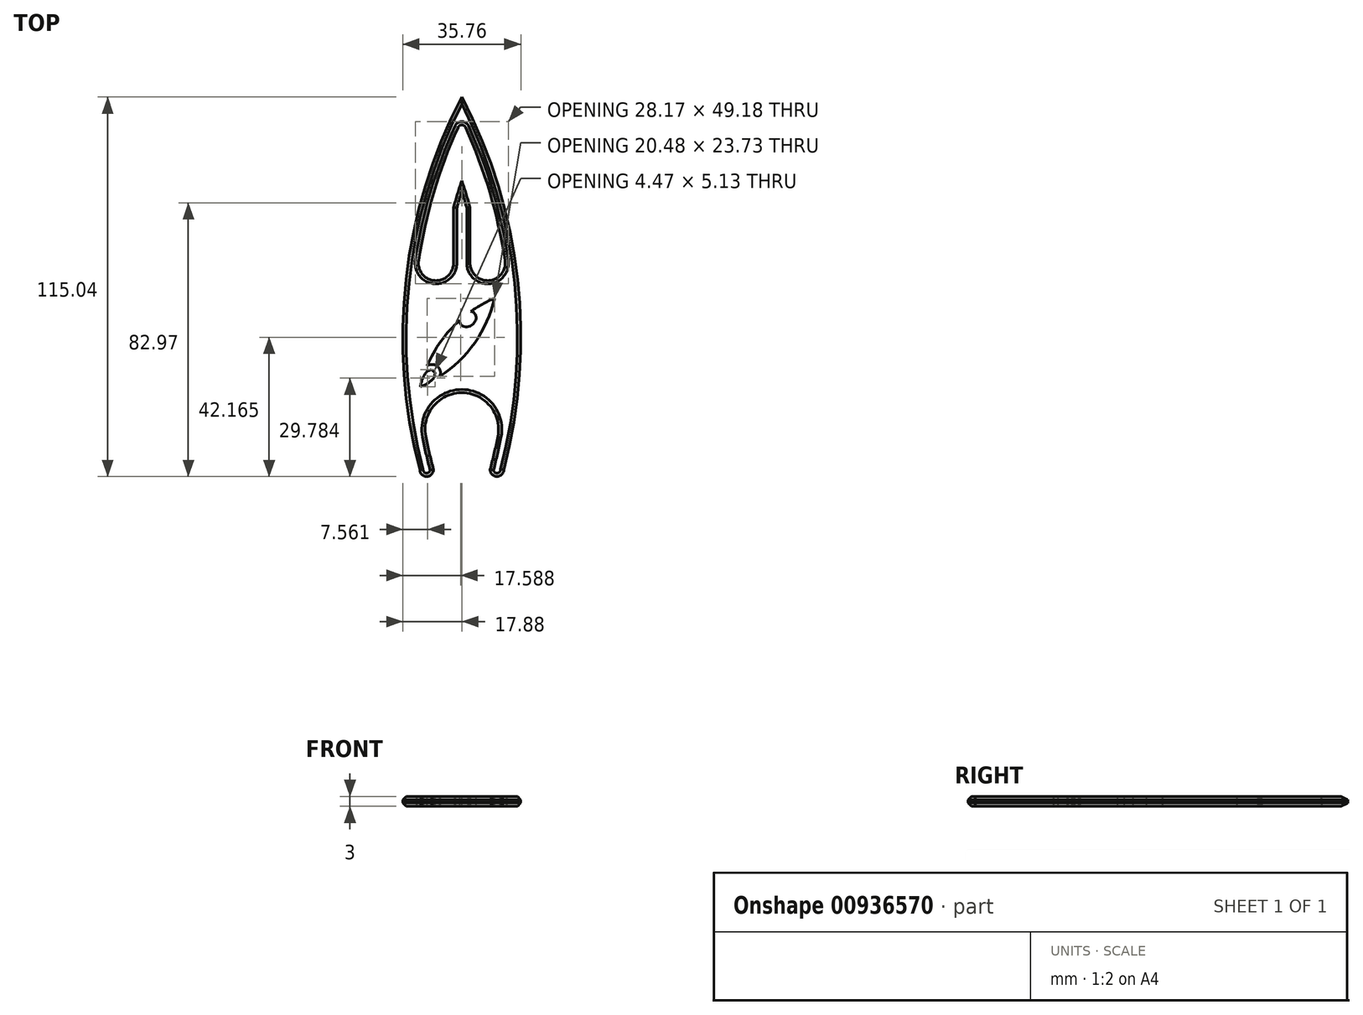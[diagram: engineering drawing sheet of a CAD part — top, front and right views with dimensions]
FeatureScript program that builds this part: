
annotation { "Feature Type Name" : "Feature", "Feature Type Description" : "" }
export const myFeature = defineFeature(function(context is Context, id is Id, definition is map)
    precondition{}
    {
        {
            var Q0;
            Q0=qCreatedBy(makeId("Top.planeOp"),FACE);
            var sketch = newSketch(context, id + "F0", { "sketchPlane" : qUnion([Q0])});
            skLineSegment(sketch, "E0.bottom", {"start": v(15, -30) * mm, "end": v(-15, -30) * mm, "construction": true});
            skLineSegment(sketch, "E0.top", {"start": v(15, 30) * mm, "end": v(11.94, 30) * mm, "construction": true});
            skLineSegment(sketch, "E0.left", {"start": v(15, -30) * mm, "end": v(15, 30) * mm, "construction": true});
            skLineSegment(sketch, "E0.right", {"start": v(-15, -30) * mm, "end": v(-15, 5.08) * mm, "construction": true});
            skPoint(sketch, "E0.middle", {"position": v(0, 0) * mm});
            skArc(sketch, "E1", {"start": v(0, -72.97) * mm, "mid": v(7.29, -56.84) * mm, "end": v(12.73, -40) * mm, "construction": true});
            skPoint(sketch, "E2", {"position": v(0, -72.97) * mm});
            skPoint(sketch, "E3", {"position": v(0, 72.97) * mm});
            skLineSegment(sketch, "E4", {"start": v(0, -30) * mm, "end": v(0, 30) * mm, "construction": true});
            skArc(sketch, "E5.MirrorCS", {"start": v(0, -72.97) * mm, "mid": v(-7.29, -56.84) * mm, "end": v(-12.73, -40) * mm, "construction": true});
            skArc(sketch, "E6", {"start": v(15, 30) * mm, "mid": v(9.06, 52.03) * mm, "end": v(0, 72.97) * mm});
            skLineSegment(sketch, "E7", {"start": v(-15, 30) * mm, "end": v(-15, 30) * mm});
            skArc(sketch, "E8", {"start": v(15, -30) * mm, "mid": v(17.88, 0) * mm, "end": v(15, 30) * mm});
            skArc(sketch, "E9", {"start": v(-15, -30) * mm, "mid": v(-17.88, 0) * mm, "end": v(-15, 30) * mm});
            skArc(sketch, "E10", {"start": v(-15, 30) * mm, "mid": v(-9.06, 52.03) * mm, "end": v(0, 72.97) * mm});
            skArc(sketch, "E11.0", {"start": v(-11.94, 30) * mm, "mid": v(-11.4, 32.6) * mm, "end": v(-10.83, 35.18) * mm, "construction": true});
            skArc(sketch, "E11.1", {"start": v(11.94, 30) * mm, "mid": v(11.4, 32.6) * mm, "end": v(10.83, 35.18) * mm, "construction": true});
            skArc(sketch, "E12.0", {"start": v(-2.5, 39.51) * mm, "mid": v(-1.3, 43.58) * mm, "end": v(0, 47.62) * mm});
            skArc(sketch, "E12.1", {"start": v(2.5, 39.51) * mm, "mid": v(1.3, 43.58) * mm, "end": v(0, 47.62) * mm});
            skLineSegment(sketch, "E13", {"start": v(2.5, 30) * mm, "end": v(2.5, 34.22) * mm, "construction": true});
            skLineSegment(sketch, "E14.MirrorCS", {"start": v(-2.5, 30) * mm, "end": v(-2.5, 34.22) * mm, "construction": true});
            skLineSegment(sketch, "E15", {"start": v(-10.83, 35.18) * mm, "end": v(-10.83, 35.18) * mm});
            skLineSegment(sketch, "E16", {"start": v(-6.72, 30) * mm, "end": v(-11.94, 30) * mm, "construction": true});
            skArc(sketch, "E17", {"start": v(-10.83, 35.18) * mm, "mid": v(-7.2, 30.03) * mm, "end": v(-2.5, 34.22) * mm, "construction": true});
            skLineSegment(sketch, "E18", {"start": v(-11.94, 30) * mm, "end": v(-15, 30) * mm, "construction": true});
            skLineSegment(sketch, "E19", {"start": v(-2.5, 30) * mm, "end": v(-6.72, 30) * mm, "construction": true});
            skArc(sketch, "E20", {"start": v(-13.22, 22.62) * mm, "mid": v(-8.61, 43.6) * mm, "end": v(-1.15, 63.75) * mm});
            skLineSegment(sketch, "E21", {"start": v(-2.5, 22.62) * mm, "end": v(-2.5, 39.51) * mm});
            skLineSegment(sketch, "E22", {"start": v(2.5, 30) * mm, "end": v(-2.5, 30) * mm, "construction": true});
            skLineSegment(sketch, "E23", {"start": v(11.94, 30) * mm, "end": v(2.5, 30) * mm, "construction": true});
            skArc(sketch, "E24.MirrorCS", {"start": v(10.83, 35.18) * mm, "mid": v(7.2, 30.03) * mm, "end": v(2.5, 34.22) * mm, "construction": true});
            skLineSegment(sketch, "E25", {"start": v(2.5, 22.62) * mm, "end": v(2.5, 39.51) * mm});
            skArc(sketch, "E26", {"start": v(13.22, 22.62) * mm, "mid": v(8.61, 43.6) * mm, "end": v(1.15, 63.75) * mm});
            skArc(sketch, "E27", {"start": v(1.15, 63.75) * mm, "mid": v(0, 64.5) * mm, "end": v(-1.15, 63.75) * mm});
            skArc(sketch, "E28", {"start": v(-1.15, 63.75) * mm, "mid": v(-0.58, 65) * mm, "end": v(0, 66.23) * mm, "construction": true});
            skArc(sketch, "E29", {"start": v(1.15, 63.75) * mm, "mid": v(0.58, 65) * mm, "end": v(0, 66.23) * mm, "construction": true});
            skLineSegment(sketch, "E30", {"start": v(12.73, -40) * mm, "end": v(8.59, -40) * mm, "construction": true});
            skArc(sketch, "E31", {"start": v(-12.73, -40) * mm, "mid": v(-13.94, -35.02) * mm, "end": v(-15, -30) * mm});
            skArc(sketch, "E32", {"start": v(12.73, -40) * mm, "mid": v(13.94, -35.02) * mm, "end": v(15, -30) * mm});
            skArc(sketch, "E33.0", {"start": v(-8.59, -40) * mm, "mid": v(-9.84, -35.02) * mm, "end": v(-10.92, -30) * mm});
            skArc(sketch, "E34.MirrorCS", {"start": v(8.59, -40) * mm, "mid": v(9.84, -35.02) * mm, "end": v(10.92, -30) * mm});
            skLineSegment(sketch, "E35", {"start": v(-8.59, -40) * mm, "end": v(-12.73, -40) * mm, "construction": true});
            skLineSegment(sketch, "E36", {"start": v(8.59, -40) * mm, "end": v(-8.59, -40) * mm, "construction": true});
            skArc(sketch, "E37", {"start": v(-12.73, -40) * mm, "mid": v(-10.66, -42.07) * mm, "end": v(-8.59, -40) * mm});
            skArc(sketch, "E38", {"start": v(8.59, -40) * mm, "mid": v(10.66, -42.07) * mm, "end": v(12.73, -40) * mm});
            skArc(sketch, "E39", {"start": v(10.92, -30) * mm, "mid": v(0, -16.7) * mm, "end": v(-10.92, -30) * mm});
            skLineSegment(sketch, "E40", {"start": v(-15, 5.08) * mm, "end": v(-15, 40.16) * mm, "construction": true});
            skLineSegment(sketch, "E41", {"start": v(-15, 22.62) * mm, "end": v(15, 22.62) * mm, "construction": true});
            skArc(sketch, "E42", {"start": v(-13.1, 23.42) * mm, "mid": v(-8.23, 17.3) * mm, "end": v(-2.5, 22.62) * mm});
            skArc(sketch, "E43.MirrorCS", {"start": v(13.1, 23.42) * mm, "mid": v(8.23, 17.3) * mm, "end": v(2.5, 22.62) * mm});
            skLineSegment(sketch, "E44", {"start": v(-10.66, -42.07) * mm, "end": v(10.66, -42.07) * mm, "construction": true});
            skSolve(sketch);
        }
        {
            var Q0;
            Q0=makeQuery(id+"F0.imprint","IMPRINT",FACE,{"disambiguationData":[TD([[makeQuery(id+"F0.imprint","IMPRINT",EDGE,{"derivedFrom":sQuery(id+"F0.wireOp",EDGE,"E6")}),1.0]])]});
            extrude(context, id + "F1", {"entities" : qUnion([Q0]), "depth" : 3 * mm, "offsetDistance" : 25 * mm});
        }
        {
            var Q0;
            Q0=makeQuery(id+"F1.opExtrude","CAP_FACE",FACE,{"disambiguationData":[OSD([sQuery(id+"F0.wireOp",EDGE,"E6"),sQuery(id+"F0.wireOp",EDGE,"E8"),sQuery(id+"F0.wireOp",EDGE,"E9"),sQuery(id+"F0.wireOp",EDGE,"E10"),sQuery(id+"F0.wireOp",EDGE,"E12.0"),sQuery(id+"F0.wireOp",EDGE,"E12.1"),sQuery(id+"F0.wireOp",EDGE,"E20"),sQuery(id+"F0.wireOp",EDGE,"E21"),sQuery(id+"F0.wireOp",EDGE,"E25"),sQuery(id+"F0.wireOp",EDGE,"E26"),sQuery(id+"F0.wireOp",EDGE,"E27"),sQuery(id+"F0.wireOp",EDGE,"E31"),sQuery(id+"F0.wireOp",EDGE,"E32"),sQuery(id+"F0.wireOp",EDGE,"E33.0"),sQuery(id+"F0.wireOp",EDGE,"E34.MirrorCS"),sQuery(id+"F0.wireOp",EDGE,"E37"),sQuery(id+"F0.wireOp",EDGE,"E38"),sQuery(id+"F0.wireOp",EDGE,"E39"),sQuery(id+"F0.wireOp",EDGE,"E42"),sQuery(id+"F0.wireOp",EDGE,"E43.MirrorCS")])],"isStart":false});
            var Q1;
            Q1=makeQuery(id+"F1.opExtrude","CAP_FACE",FACE,{"disambiguationData":[OSD([sQuery(id+"F0.wireOp",EDGE,"E6"),sQuery(id+"F0.wireOp",EDGE,"E8"),sQuery(id+"F0.wireOp",EDGE,"E9"),sQuery(id+"F0.wireOp",EDGE,"E10"),sQuery(id+"F0.wireOp",EDGE,"E12.0"),sQuery(id+"F0.wireOp",EDGE,"E12.1"),sQuery(id+"F0.wireOp",EDGE,"E20"),sQuery(id+"F0.wireOp",EDGE,"E21"),sQuery(id+"F0.wireOp",EDGE,"E25"),sQuery(id+"F0.wireOp",EDGE,"E26"),sQuery(id+"F0.wireOp",EDGE,"E27"),sQuery(id+"F0.wireOp",EDGE,"E31"),sQuery(id+"F0.wireOp",EDGE,"E32"),sQuery(id+"F0.wireOp",EDGE,"E33.0"),sQuery(id+"F0.wireOp",EDGE,"E34.MirrorCS"),sQuery(id+"F0.wireOp",EDGE,"E37"),sQuery(id+"F0.wireOp",EDGE,"E38"),sQuery(id+"F0.wireOp",EDGE,"E39"),sQuery(id+"F0.wireOp",EDGE,"E42"),sQuery(id+"F0.wireOp",EDGE,"E43.MirrorCS")])],"isStart":true});
            chamfer(context, id + "F2", {"entities" : qUnion([Q0, Q1]), "width" : 1 * mm, "tangentPropagation" : true});
        }
        {
            var Q0;
            Q0=makeQuery(id+"F1.opExtrude","CAP_FACE",FACE,{"disambiguationData":[OSD([sQuery(id+"F0.wireOp",EDGE,"E6"),sQuery(id+"F0.wireOp",EDGE,"E8"),sQuery(id+"F0.wireOp",EDGE,"E9"),sQuery(id+"F0.wireOp",EDGE,"E10"),sQuery(id+"F0.wireOp",EDGE,"E12.0"),sQuery(id+"F0.wireOp",EDGE,"E12.1"),sQuery(id+"F0.wireOp",EDGE,"E20"),sQuery(id+"F0.wireOp",EDGE,"E21"),sQuery(id+"F0.wireOp",EDGE,"E25"),sQuery(id+"F0.wireOp",EDGE,"E26"),sQuery(id+"F0.wireOp",EDGE,"E27"),sQuery(id+"F0.wireOp",EDGE,"E31"),sQuery(id+"F0.wireOp",EDGE,"E32"),sQuery(id+"F0.wireOp",EDGE,"E33.0"),sQuery(id+"F0.wireOp",EDGE,"E34.MirrorCS"),sQuery(id+"F0.wireOp",EDGE,"E37"),sQuery(id+"F0.wireOp",EDGE,"E38"),sQuery(id+"F0.wireOp",EDGE,"E39"),sQuery(id+"F0.wireOp",EDGE,"E42"),sQuery(id+"F0.wireOp",EDGE,"E43.MirrorCS")])],"isStart":false});
            var sketch = newSketch(context, id + "F3", { "sketchPlane" : qUnion([Q0])});
            skEllipticalArc(sketch, "E45", {});
            skArc(sketch, "E46", {"start": v(9.95, 11.96) * mm, "mid": v(6.24, 10.15) * mm, "end": v(2.76, 7.96) * mm});
            skLineSegment(sketch, "E47", {"start": v(-10.52, -10.21) * mm, "end": v(-9.18, -9.72) * mm});
            skArc(sketch, "E48", {"start": v(-6.74, -11.77) * mm, "mid": v(-7.4, -8.7) * mm, "end": v(-10.53, -8.59) * mm});
            skArc(sketch, "E49", {"start": v(-10.52, -10.21) * mm, "mid": v(-11.87, -12.38) * mm, "end": v(-12.55, -14.85) * mm});
            skLineSegment(sketch, "E50", {"start": v(-9.18, -9.72) * mm, "end": v(-8.09, -10.64) * mm});
            skLineSegment(sketch, "E51", {"start": v(-8.09, -10.64) * mm, "end": v(-8.33, -12.05) * mm});
            skArc(sketch, "E52", {"start": v(-0.63, 5.27) * mm, "mid": v(-6.35, -1.1) * mm, "end": v(-10.53, -8.59) * mm});
            skArc(sketch, "E53", {"start": v(-6.74, -11.77) * mm, "mid": v(3.92, -1.53) * mm, "end": v(9.95, 11.96) * mm});
            skArc(sketch, "E54", {"start": v(-12.55, -14.85) * mm, "mid": v(-10.24, -13.75) * mm, "end": v(-8.33, -12.05) * mm});
            skLineSegment(sketch, "E55", {"start": v(9.95, 11.96) * mm, "end": v(-12.55, -14.85) * mm, "construction": true});
            skPoint(sketch, "E56", {"position": v(-1.3, -1.44) * mm});
            const initialGuessF3  = {"E45": [0.0018648564444938092, 0.005612928984472541, 0.7863707315562493, 0.6177548644500417, 0.0026833365175593688, 0.0021557519960715924, 2.513682, 0.6416826928204069]};
            skSetInitialGuess(sketch, initialGuessF3);
            skSolve(sketch);
        }
        {
            var Q0;
            Q0=makeQuery(id+"F3.imprint","IMPRINT",FACE,{"disambiguationData":[TD([[makeQuery(id+"F3.imprint","IMPRINT",EDGE,{"derivedFrom":sQuery(id+"F3.wireOp",EDGE,"E45")}),-1.0]])]});
            var Q1;
            Q1=makeQuery(id+"F3.imprint","IMPRINT",FACE,{"disambiguationData":[TD([[makeQuery(id+"F3.imprint","IMPRINT",EDGE,{"derivedFrom":sQuery(id+"F3.wireOp",EDGE,"E47")}),-1.0]])]});
            extrude(context, id + "F4", {"entities" : qUnion([Q0, Q1]), "operationType" : NewBodyOperationType.REMOVE, "oppositeDirection" : true, "depth" : 25 * mm, "offsetDistance" : 25 * mm});
        }
    });
